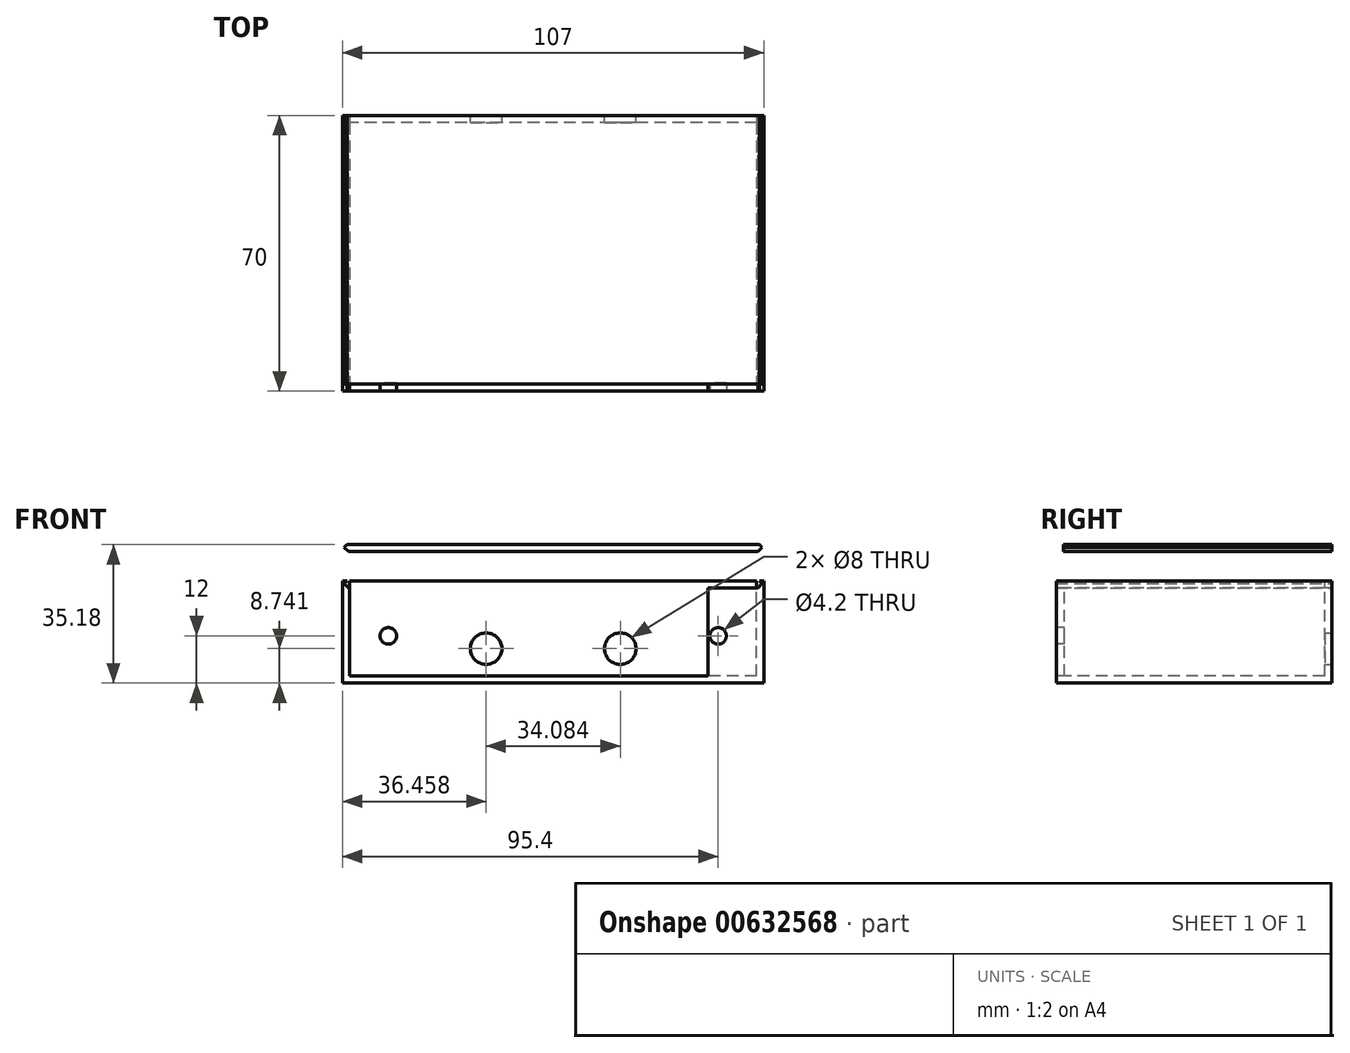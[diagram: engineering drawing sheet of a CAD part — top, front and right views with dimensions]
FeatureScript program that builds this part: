
annotation { "Feature Type Name" : "Feature", "Feature Type Description" : "" }
export const myFeature = defineFeature(function(context is Context, id is Id, definition is map)
    precondition{}
    {
        {
            var Q0;
            Q0=qCreatedBy(makeId("Front.planeOp"),FACE);
            var sketch = newSketch(context, id + "F0", { "sketchPlane" : qUnion([Q0])});
            skLineSegment(sketch, "E0", {"start": v(0, 0) * mm, "end": v(53.5, 0) * mm});
            skLineSegment(sketch, "E1", {"start": v(53.5, 0) * mm, "end": v(53.5, 26) * mm});
            skLineSegment(sketch, "E2", {"start": v(53.5, 26) * mm, "end": v(0, 26) * mm});
            skLineSegment(sketch, "E3.MirrorCS", {"start": v(-53.5, 26) * mm, "end": v(0, 26) * mm});
            skLineSegment(sketch, "E4.MirrorCS", {"start": v(-53.5, 0) * mm, "end": v(-53.5, 26) * mm});
            skLineSegment(sketch, "E5.MirrorCS", {"start": v(0, 0) * mm, "end": v(-53.5, 0) * mm});
            skLineSegment(sketch, "E6", {"start": v(41.9, 0) * mm, "end": v(41.9, 12) * mm, "construction": true});
            skCircle(sketch, "E7", {"center": v(41.9, 12) * mm, "radius": 2.1 * mm});
            skCircle(sketch, "E8.MirrorC", {"center": v(-41.9, 12) * mm, "radius": 2.1 * mm});
            skLineSegment(sketch, "E9", {"start": v(39.3, 0) * mm, "end": v(39.3, 26) * mm});
            skLineSegment(sketch, "E10.0", {"start": v(-51.7, 1.8) * mm, "end": v(-51.7, 24.2) * mm});
            skLineSegment(sketch, "E10.1", {"start": v(51.7, 24.2) * mm, "end": v(0, 24.2) * mm});
            skLineSegment(sketch, "E10.2", {"start": v(51.7, 1.8) * mm, "end": v(51.7, 24.2) * mm});
            skLineSegment(sketch, "E10.3", {"start": v(-51.7, 24.2) * mm, "end": v(0, 24.2) * mm});
            skLineSegment(sketch, "E10.4", {"start": v(0, 1.8) * mm, "end": v(51.7, 1.8) * mm});
            skLineSegment(sketch, "E10.5", {"start": v(0, 1.8) * mm, "end": v(-51.7, 1.8) * mm});
            skLineSegment(sketch, "E11.MirrorCS", {"start": v(-39.3, 0) * mm, "end": v(-39.3, 26) * mm});
            skSolve(sketch);
        }
        {
            var Q0;
            {var subQ1=sQuery(id+"F0.wireOp",EDGE,"E4.MirrorCS");Q0=makeQuery(id+"F0.imprint","IMPRINT",FACE,{"disambiguationData":[TD([[makeQuery(id+"F0.imprint","IMPRINT",EDGE,{"derivedFrom":subQ1}),-1.0]])]});}
            var Q1;
            {var subQ5=sQuery(id+"F0.wireOp",EDGE,"E3.MirrorCS");var subQ6=sQuery(id+"F0.wireOp",EDGE,"E2");var subQ7=makeQuery(id+"F0.imprint","INTERSECT",VERTEX,{"derivedFrom":[subQ6,subQ5]});Q1=makeQuery(id+"F0.imprint","IMPRINT",FACE,{"disambiguationData":[TD([[makeQuery(id+"F0.imprint","IMPRINT",EDGE,{"disambiguationData":[TD([[subQ7,1.0]])],"derivedFrom":subQ6}),1.0]])]});}
            var Q2;
            {var subQ5=sQuery(id+"F0.wireOp",EDGE,"E0");var subQ9=sQuery(id+"F0.wireOp",EDGE,"E5.MirrorCS");var subQ10=makeQuery(id+"F0.imprint","INTERSECT",VERTEX,{"derivedFrom":[subQ5,subQ9]});Q2=makeQuery(id+"F0.imprint","IMPRINT",FACE,{"disambiguationData":[TD([[makeQuery(id+"F0.imprint","IMPRINT",EDGE,{"disambiguationData":[TD([[subQ10,-1.0]])],"derivedFrom":subQ5}),1.0]])]});}
            var Q3;
            {var subQ1=sQuery(id+"F0.wireOp",EDGE,"E1");Q3=makeQuery(id+"F0.imprint","IMPRINT",FACE,{"disambiguationData":[TD([[makeQuery(id+"F0.imprint","IMPRINT",EDGE,{"derivedFrom":subQ1}),1.0]])]});}
            extrude(context, id + "F1", {"entities" : qUnion([Q0, Q1, Q2, Q3]), "oppositeDirection" : true, "depth" : 70 * mm, "offsetDistance" : 25 * mm});
        }
        {
            var Q0;
            Q0=makeQuery(id+"F0.imprint","IMPRINT",FACE,{"disambiguationData":[TD([[makeQuery(id+"F0.imprint","IMPRINT",EDGE,{"derivedFrom":sQuery(id+"F0.wireOp",EDGE,"E7")}),-1.0]])]});
            var Q1;
            Q1=makeQuery(id+"F0.imprint","IMPRINT",FACE,{"disambiguationData":[TD([[makeQuery(id+"F0.imprint","IMPRINT",EDGE,{"derivedFrom":sQuery(id+"F0.wireOp",EDGE,"E8.MirrorC")}),1.0]])]});
            extrude(context, id + "F2", {"entities" : qUnion([Q0, Q1]), "operationType" : NewBodyOperationType.ADD, "oppositeDirection" : true, "depth" : 2 * mm, "offsetDistance" : 25 * mm});
        }
        {
            var Q0;
            Q0=makeQuery(id+"F1.opExtrude","CAP_FACE",FACE,{"disambiguationData":[OSD([sQuery(id+"F0.wireOp",EDGE,"E0"),sQuery(id+"F0.wireOp",EDGE,"E1"),sQuery(id+"F0.wireOp",EDGE,"E2"),sQuery(id+"F0.wireOp",EDGE,"E3.MirrorCS"),sQuery(id+"F0.wireOp",EDGE,"E4.MirrorCS"),sQuery(id+"F0.wireOp",EDGE,"E5.MirrorCS"),sQuery(id+"F0.wireOp",EDGE,"E10.0"),sQuery(id+"F0.wireOp",EDGE,"E10.1"),sQuery(id+"F0.wireOp",EDGE,"E10.2"),sQuery(id+"F0.wireOp",EDGE,"E10.3"),sQuery(id+"F0.wireOp",EDGE,"E10.4"),sQuery(id+"F0.wireOp",EDGE,"E10.5")])],"isStart":false});
            cPlane(context, id + "F3", {"entities" : qUnion([Q0]), "cplaneType" : CPlaneType.OFFSET, "offset" : 0 * mm, "width" : 150 * mm, "height" : 150 * mm});
        }
        {
            var Q0;
            Q0=qCreatedBy(id+"F3.planeOp",FACE);
            var sketch = newSketch(context, id + "F4", { "sketchPlane" : qUnion([Q0])});
            skLineSegment(sketch, "E12", {"start": v(0, 26) * mm, "end": v(52.4, 26) * mm});
            skLineSegment(sketch, "E13", {"start": v(0, 24.2) * mm, "end": v(52, 24.2) * mm});
            skLineSegment(sketch, "E14", {"start": v(52, 24.2) * mm, "end": v(53.1, 25.3) * mm});
            skLineSegment(sketch, "E15", {"start": v(53.1, 25.3) * mm, "end": v(52.4, 26) * mm});
            skLineSegment(sketch, "E16", {"start": v(52.4, 26) * mm, "end": v(53.2, 26) * mm, "construction": true});
            skLineSegment(sketch, "E17", {"start": v(52, 24.2) * mm, "end": v(53.1, 24.2) * mm, "construction": true});
            skLineSegment(sketch, "E18.MirrorCS", {"start": v(0, 26) * mm, "end": v(-52.4, 26) * mm});
            skLineSegment(sketch, "E19.MirrorCS", {"start": v(0, 24.2) * mm, "end": v(-52, 24.2) * mm});
            skLineSegment(sketch, "E20.MirrorCS", {"start": v(-52, 24.2) * mm, "end": v(-53.1, 25.3) * mm});
            skLineSegment(sketch, "E21.MirrorCS", {"start": v(-53.1, 25.3) * mm, "end": v(-52.4, 26) * mm});
            skLineSegment(sketch, "E22", {"start": v(0, 33.39) * mm, "end": v(52, 33.39) * mm});
            skLineSegment(sketch, "E23", {"start": v(0, 35.18) * mm, "end": v(52.4, 35.18) * mm});
            skLineSegment(sketch, "E24", {"start": v(52.4, 35.18) * mm, "end": v(53.1, 34.48) * mm});
            skLineSegment(sketch, "E25", {"start": v(52, 33.39) * mm, "end": v(53.1, 34.48) * mm});
            skLineSegment(sketch, "E26", {"start": v(52.4, 35.18) * mm, "end": v(56.43, 35.18) * mm, "construction": true});
            skLineSegment(sketch, "E27", {"start": v(52, 33.39) * mm, "end": v(55.57, 33.39) * mm, "construction": true});
            skLineSegment(sketch, "E28.MirrorCS", {"start": v(0, 35.18) * mm, "end": v(-52.4, 35.18) * mm});
            skLineSegment(sketch, "E29.MirrorCS", {"start": v(0, 33.39) * mm, "end": v(-52, 33.39) * mm});
            skLineSegment(sketch, "E30.MirrorCS", {"start": v(-52, 33.39) * mm, "end": v(-53.1, 34.48) * mm});
            skLineSegment(sketch, "E31.MirrorCS", {"start": v(-52.4, 35.18) * mm, "end": v(-53.1, 34.48) * mm});
            skSolve(sketch);
        }
        {
            var Q0;
            Q0=makeQuery(id+"F4.imprint","IMPRINT",FACE,{"disambiguationData":[TD([[makeQuery(id+"F4.imprint","IMPRINT",EDGE,{"derivedFrom":sQuery(id+"F4.wireOp",EDGE,"E12")}),-1.0]])]});
            extrude(context, id + "F5", {"entities" : qUnion([Q0]), "operationType" : NewBodyOperationType.REMOVE, "oppositeDirection" : true, "depth" : 70 * mm, "offsetDistance" : 25 * mm});
        }
        {
            var Q0;
            Q0=makeQuery(id+"F4.imprint","IMPRINT",FACE,{"disambiguationData":[TD([[makeQuery(id+"F4.imprint","IMPRINT",EDGE,{"derivedFrom":sQuery(id+"F4.wireOp",EDGE,"E22")}),1.0]])]});
            extrude(context, id + "F6", {"entities" : qUnion([Q0]), "oppositeDirection" : true, "depth" : 68.2 * mm, "offsetDistance" : 25 * mm});
        }
        {
            var Q0;
            Q0=makeQuery(id+"F1.opExtrude","CAP_FACE",FACE,{"disambiguationData":[OSD([sQuery(id+"F0.wireOp",EDGE,"E0"),sQuery(id+"F0.wireOp",EDGE,"E1"),sQuery(id+"F0.wireOp",EDGE,"E2"),sQuery(id+"F0.wireOp",EDGE,"E3.MirrorCS"),sQuery(id+"F0.wireOp",EDGE,"E4.MirrorCS"),sQuery(id+"F0.wireOp",EDGE,"E5.MirrorCS"),sQuery(id+"F0.wireOp",EDGE,"E10.0"),sQuery(id+"F0.wireOp",EDGE,"E10.1"),sQuery(id+"F0.wireOp",EDGE,"E10.2"),sQuery(id+"F0.wireOp",EDGE,"E10.3"),sQuery(id+"F0.wireOp",EDGE,"E10.4"),sQuery(id+"F0.wireOp",EDGE,"E10.5")])],"isStart":false});
            var sketch = newSketch(context, id + "F7", { "sketchPlane" : qUnion([Q0])});
            skLineSegment(sketch, "E32", {"start": v(0, 1.8) * mm, "end": v(51.7, 1.8) * mm});
            skLineSegment(sketch, "E33", {"start": v(51.7, 1.8) * mm, "end": v(51.7, 26) * mm});
            skLineSegment(sketch, "E34", {"start": v(51.7, 26) * mm, "end": v(0, 26) * mm});
            skLineSegment(sketch, "E35", {"start": v(51.7, 26) * mm, "end": v(53.5, 26) * mm});
            skLineSegment(sketch, "E36", {"start": v(53.5, 26) * mm, "end": v(53.5, 23.88) * mm});
            skLineSegment(sketch, "E37", {"start": v(53.5, 23.88) * mm, "end": v(51.7, 23.88) * mm});
            skLineSegment(sketch, "E38.MirrorCS", {"start": v(-51.7, 26) * mm, "end": v(0, 26) * mm});
            skLineSegment(sketch, "E39.MirrorCS", {"start": v(-51.7, 26) * mm, "end": v(-53.5, 26) * mm});
            skLineSegment(sketch, "E40.MirrorCS", {"start": v(-53.5, 26) * mm, "end": v(-53.5, 23.88) * mm});
            skLineSegment(sketch, "E41.MirrorCS", {"start": v(-53.5, 23.88) * mm, "end": v(-51.7, 23.88) * mm});
            skLineSegment(sketch, "E42.MirrorCS", {"start": v(-51.7, 1.8) * mm, "end": v(-51.7, 26) * mm});
            skLineSegment(sketch, "E43.MirrorCS", {"start": v(0, 1.8) * mm, "end": v(-51.7, 1.8) * mm});
            skCircle(sketch, "E44", {"center": v(-17.04, 8.74) * mm, "radius": 4 * mm});
            skCircle(sketch, "E45.MirrorC", {"center": v(17.04, 8.74) * mm, "radius": 4 * mm});
            skSolve(sketch);
        }
        {
            var Q0;
            {var subQ13=sQuery(id+"F7.wireOp",EDGE,"E32");Q0=makeQuery(id+"F7.imprint","IMPRINT",FACE,{"disambiguationData":[TD([[makeQuery(id+"F7.imprint","IMPRINT",EDGE,{"derivedFrom":subQ13}),1.0]])]});}
            var Q1;
            {var subQ1=sQuery(id+"F7.wireOp",EDGE,"E40.MirrorCS");Q1=makeQuery(id+"F7.imprint","IMPRINT",FACE,{"disambiguationData":[TD([[makeQuery(id+"F7.imprint","IMPRINT",EDGE,{"derivedFrom":subQ1}),-1.0]])]});}
            var Q2;
            {var subQ5=sQuery(id+"F4.wireOp",EDGE,"E20.MirrorCS");Q2=makeQuery(id+"F7.imprint","IMPRINT",FACE,{"disambiguationData":[TD([[makeQuery(id+"F7.imprint","IMPRINT",EDGE,{"derivedFrom":makeQuery(id+"F5.boolean.opBoolean","COPY",EDGE,{"derivedFrom":makeQuery(id+"F5.opExtrude","CAP_EDGE",EDGE,{"disambiguationData":[OSD([subQ5])],"isStart":true})})}),-1.0]])]});}
            var Q3;
            {var subQ0=sQuery(id+"F7.wireOp",EDGE,"E36");Q3=makeQuery(id+"F7.imprint","IMPRINT",FACE,{"disambiguationData":[TD([[makeQuery(id+"F7.imprint","IMPRINT",EDGE,{"derivedFrom":subQ0}),1.0]])]});}
            var Q4;
            {var subQ5=sQuery(id+"F4.wireOp",EDGE,"E14");Q4=makeQuery(id+"F7.imprint","IMPRINT",FACE,{"disambiguationData":[TD([[makeQuery(id+"F7.imprint","IMPRINT",EDGE,{"derivedFrom":makeQuery(id+"F5.boolean.opBoolean","COPY",EDGE,{"derivedFrom":makeQuery(id+"F5.opExtrude","CAP_EDGE",EDGE,{"disambiguationData":[OSD([subQ5])],"isStart":true})})}),1.0]])]});}
            extrude(context, id + "F8", {"entities" : qUnion([Q0, Q1, Q2, Q3, Q4]), "operationType" : NewBodyOperationType.ADD, "oppositeDirection" : true, "depth" : 1.8 * mm, "offsetDistance" : 25 * mm});
        }
    });
